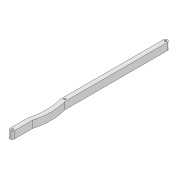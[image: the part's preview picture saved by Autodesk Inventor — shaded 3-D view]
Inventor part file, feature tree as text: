
AUTODESK INVENTOR PART (.ipt)
format: ipt  version: 2022 (Build 260153000, 153)  size: 99,840 bytes
history: native  units: mm
features: extrude x1, sketch x1
ambient origin geometry x8: Origin, YZ Plane, XZ Plane, XY Plane, X Axis, Y Axis, Z Axis, Center Point
bodies: Solid1 (feature_tree)
feature tree (2):
  extrude  "Extrusion1"  Depth=212.266mm
  sketch  "Sketch1"  dims[d0=6.0mm d1=212.266mm d2=3.0mm d3=3.0mm d4=10.0mm d5=0.0mm d10=3.0mm d11=72.721mm d12=80.0mm d13=80.0mm d14=3.0mm d15=25.0mm]
